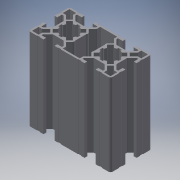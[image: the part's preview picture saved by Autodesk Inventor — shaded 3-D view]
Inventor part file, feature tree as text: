
AUTODESK INVENTOR PART (.ipt)
format: ipt  version: 2018 (Build 220112000, 112)  size: 573,952 bytes
history: native  units: mm
features: other x1, extrude x1, sketch x1
ambient origin geometry x8: Origin, YZ Plane, XZ Plane, XY Plane, X Axis, Y Axis, Z Axis, Center Point
bodies: Body1 (feature_tree)
feature tree (3):
  other  "Sólido1"
  extrude  "Extrusão1"  [1 undecoded]
  sketch  "Esboço1"  dims[d0=60.0mm d1=0.0mm]
note: 1 required parameter value undecoded (feature->parameter linkage not recoverable at this tier; creation-order binding heuristic only, values carry confidence <= 0.55)
